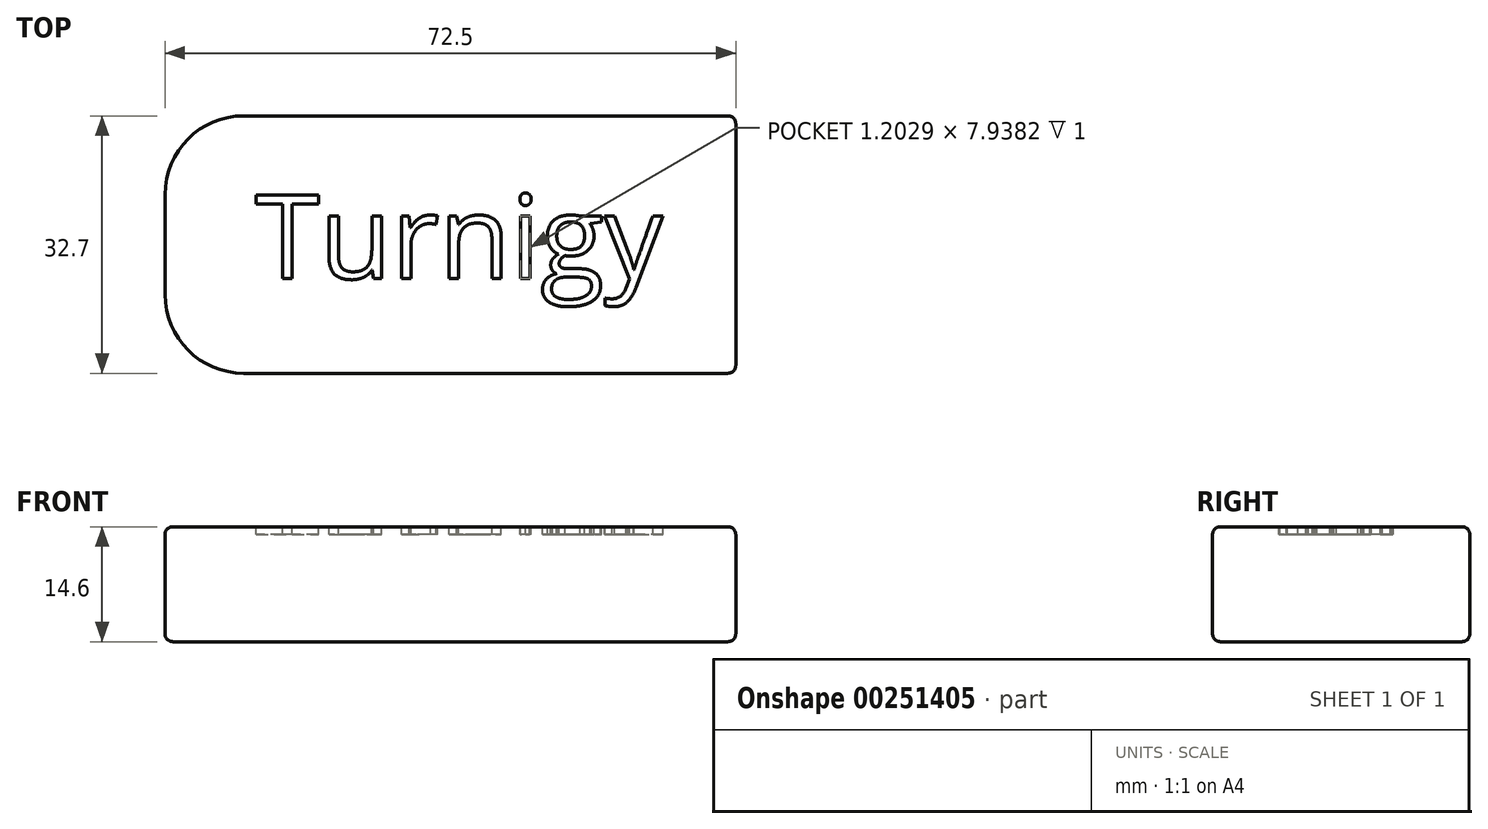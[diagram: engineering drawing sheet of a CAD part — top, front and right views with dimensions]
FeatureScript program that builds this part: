
annotation { "Feature Type Name" : "Feature", "Feature Type Description" : "" }
export const myFeature = defineFeature(function(context is Context, id is Id, definition is map)
    precondition{}
    {
        {
            var Q0;
            Q0=qCreatedBy(makeId("Top.planeOp"),FACE);
            var sketch = newSketch(context, id + "F0", { "sketchPlane" : qUnion([Q0])});
            skLineSegment(sketch, "E0.bottom", {"start": v(36.25, 16.35) * mm, "end": v(-36.25, 16.35) * mm});
            skLineSegment(sketch, "E0.top", {"start": v(36.25, -16.35) * mm, "end": v(-36.25, -16.35) * mm});
            skLineSegment(sketch, "E0.left", {"start": v(36.25, 16.35) * mm, "end": v(36.25, -16.35) * mm});
            skLineSegment(sketch, "E0.right", {"start": v(-36.25, 16.35) * mm, "end": v(-36.25, -16.35) * mm});
            skPoint(sketch, "E0.middle", {"position": v(0, 0) * mm});
            skSolve(sketch);
        }
        {
            var Q0;
            Q0=makeQuery(id+"F0.imprint","IMPRINT",FACE,{"disambiguationData":[TD([[makeQuery(id+"F0.imprint","IMPRINT",EDGE,{"derivedFrom":sQuery(id+"F0.wireOp",EDGE,"E0.bottom")}),1.0]])]});
            extrude(context, id + "F1", {"entities" : qUnion([Q0]), "depth" : 14.6 * mm, "symmetric" : true});
        }
        {
            var Q0;
            Q0=makeQuery(id+"F1.opExtrude","SWEPT_EDGE",EDGE,{"disambiguationData":[OSD([sQuery(id+"F0.wireOp",EDGE,"E0.bottom"),sQuery(id+"F0.wireOp",EDGE,"E0.right")])]});
            var Q1;
            Q1=makeQuery(id+"F1.opExtrude","SWEPT_EDGE",EDGE,{"disambiguationData":[OSD([sQuery(id+"F0.wireOp",EDGE,"E0.top"),sQuery(id+"F0.wireOp",EDGE,"E0.right")])]});
            fillet(context, id + "F2", {"entities" : qUnion([Q0, Q1]), "radius" : 10 * mm, "tangentPropagation" : true, "allowEdgeOverflow" : false});
        }
        {
            var Q0;
            Q0=makeQuery(id+"F1.opExtrude","CAP_FACE",FACE,{"disambiguationData":[OSD([sQuery(id+"F0.wireOp",EDGE,"E0.bottom"),sQuery(id+"F0.wireOp",EDGE,"E0.top"),sQuery(id+"F0.wireOp",EDGE,"E0.left"),sQuery(id+"F0.wireOp",EDGE,"E0.right")])],"isStart":false});
            var Q1;
            Q1=makeQuery(id+"F1.opExtrude","CAP_FACE",FACE,{"disambiguationData":[OSD([sQuery(id+"F0.wireOp",EDGE,"E0.bottom"),sQuery(id+"F0.wireOp",EDGE,"E0.top"),sQuery(id+"F0.wireOp",EDGE,"E0.left"),sQuery(id+"F0.wireOp",EDGE,"E0.right")])],"isStart":true});
            var Q2;
            Q2=makeQuery(id+"F1.opExtrude","SWEPT_FACE",FACE,{"disambiguationData":[OSD([sQuery(id+"F0.wireOp",EDGE,"E0.left")])]});
            fillet(context, id + "F3", {"entities" : qUnion([Q0, Q1, Q2]), "radius" : 1 * mm, "tangentPropagation" : true, "allowEdgeOverflow" : false});
        }
        {
            var Q0;
            Q0=makeQuery(id+"F1.opExtrude","CAP_FACE",FACE,{"disambiguationData":[OSD([sQuery(id+"F0.wireOp",EDGE,"E0.bottom"),sQuery(id+"F0.wireOp",EDGE,"E0.top"),sQuery(id+"F0.wireOp",EDGE,"E0.left"),sQuery(id+"F0.wireOp",EDGE,"E0.right")])],"isStart":false});
            var sketch = newSketch(context, id + "F4", { "sketchPlane" : qUnion([Q0])});
            skText(sketch, "E1", { "text": "Turnigy", "fontName": "OpenSans-Regular.ttf"});
            const initialGuessF4  = {"E1": [-0.02481, -0.00433, 1, 0, 0.01068]};
            skSetInitialGuess(sketch, initialGuessF4);
            skSolve(sketch);
        }
        {
            var Q0;
            Q0 = qSketchRegion(id + "F4", true);
            extrude(context, id + "F5", {"entities" : qUnion([Q0]), "operationType" : NewBodyOperationType.REMOVE, "oppositeDirection" : true, "depth" : 1 * mm});
        }
    });
